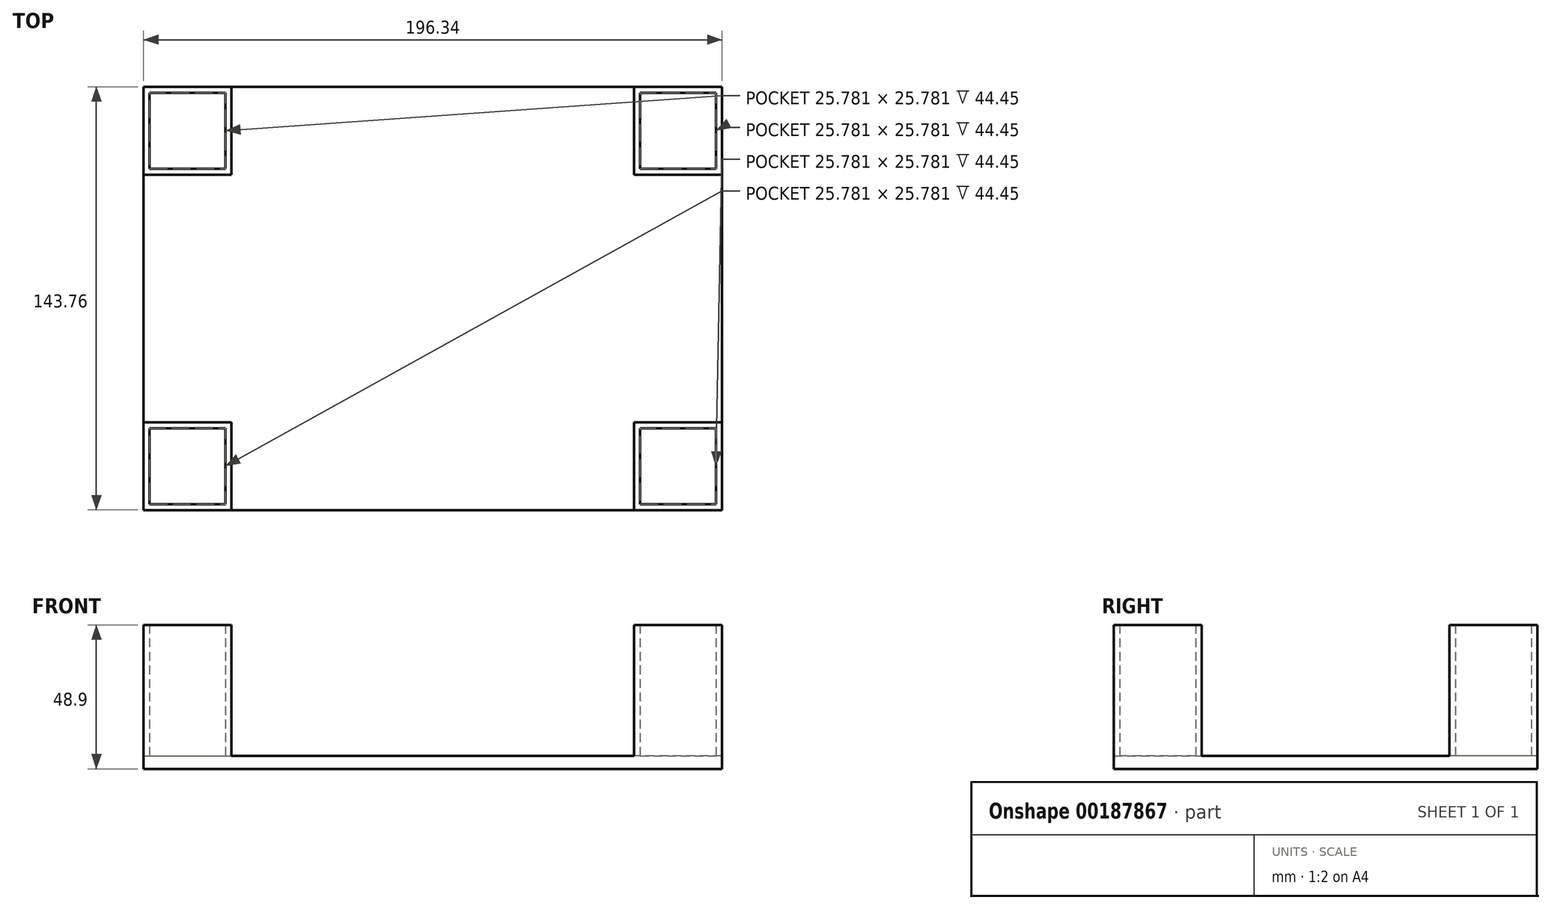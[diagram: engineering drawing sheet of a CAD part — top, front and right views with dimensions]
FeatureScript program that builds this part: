
annotation { "Feature Type Name" : "Feature", "Feature Type Description" : "" }
export const myFeature = defineFeature(function(context is Context, id is Id, definition is map)
    precondition{}
    {
        {
            var Q0;
            Q0=qCreatedBy(makeId("Top.planeOp"),FACE);
            var sketch = newSketch(context, id + "F0", { "sketchPlane" : qUnion([Q0])});
            skLineSegment(sketch, "E0.bottom", {"start": v(-88.52, 50.53) * mm, "end": v(107.82, 50.53) * mm});
            skLineSegment(sketch, "E0.top", {"start": v(-88.52, -93.23) * mm, "end": v(107.82, -93.23) * mm});
            skLineSegment(sketch, "E0.left", {"start": v(-88.52, 50.53) * mm, "end": v(-88.52, -93.23) * mm});
            skLineSegment(sketch, "E0.right", {"start": v(107.82, 50.53) * mm, "end": v(107.82, -93.23) * mm});
            skSolve(sketch);
        }
        {
            var Q0;
            Q0 = qSketchRegion(id + "F0", true);
            extrude(context, id + "F1", {"entities" : qUnion([Q0]), "depth" : 4.44 * mm});
        }
        {
            var Q0;
            Q0=makeQuery(id+"F1.opExtrude","CAP_FACE",FACE,{"disambiguationData":[OSD([sQuery(id+"F0.wireOp",EDGE,"E0.bottom"),sQuery(id+"F0.wireOp",EDGE,"E0.top"),sQuery(id+"F0.wireOp",EDGE,"E0.left"),sQuery(id+"F0.wireOp",EDGE,"E0.right")])],"isStart":false});
            var sketch = newSketch(context, id + "F2", { "sketchPlane" : qUnion([Q0])});
            skLineSegment(sketch, "E1.bottom", {"start": v(-88.52, 50.53) * mm, "end": v(-58.68, 50.53) * mm});
            skLineSegment(sketch, "E1.top", {"start": v(-88.52, 20.69) * mm, "end": v(-58.68, 20.69) * mm});
            skLineSegment(sketch, "E1.left", {"start": v(-88.52, 50.53) * mm, "end": v(-88.52, 20.69) * mm});
            skLineSegment(sketch, "E1.right", {"start": v(-58.68, 50.53) * mm, "end": v(-58.68, 20.69) * mm});
            skLineSegment(sketch, "E2.bottom", {"start": v(107.82, 50.53) * mm, "end": v(77.98, 50.53) * mm});
            skLineSegment(sketch, "E2.top", {"start": v(107.82, 20.69) * mm, "end": v(77.98, 20.69) * mm});
            skLineSegment(sketch, "E2.left", {"start": v(107.82, 50.53) * mm, "end": v(107.82, 20.69) * mm});
            skLineSegment(sketch, "E2.right", {"start": v(77.98, 50.53) * mm, "end": v(77.98, 20.69) * mm});
            skLineSegment(sketch, "E3.bottom", {"start": v(107.82, -93.23) * mm, "end": v(77.98, -93.23) * mm});
            skLineSegment(sketch, "E3.top", {"start": v(107.82, -63.39) * mm, "end": v(77.98, -63.39) * mm});
            skLineSegment(sketch, "E3.left", {"start": v(107.82, -93.23) * mm, "end": v(107.82, -63.39) * mm});
            skLineSegment(sketch, "E3.right", {"start": v(77.98, -93.23) * mm, "end": v(77.98, -63.39) * mm});
            skLineSegment(sketch, "E4.bottom", {"start": v(-88.52, -93.23) * mm, "end": v(-58.68, -93.23) * mm});
            skLineSegment(sketch, "E4.top", {"start": v(-88.52, -63.39) * mm, "end": v(-58.68, -63.39) * mm});
            skLineSegment(sketch, "E4.left", {"start": v(-88.52, -93.23) * mm, "end": v(-88.52, -63.39) * mm});
            skLineSegment(sketch, "E4.right", {"start": v(-58.68, -93.23) * mm, "end": v(-58.68, -63.39) * mm});
            skLineSegment(sketch, "E5.bottom", {"start": v(-86.49, 48.5) * mm, "end": v(-60.7, 48.5) * mm});
            skLineSegment(sketch, "E5.top", {"start": v(-86.49, 22.72) * mm, "end": v(-60.7, 22.72) * mm});
            skLineSegment(sketch, "E5.left", {"start": v(-86.49, 48.5) * mm, "end": v(-86.49, 22.72) * mm});
            skLineSegment(sketch, "E5.right", {"start": v(-60.7, 48.5) * mm, "end": v(-60.7, 22.72) * mm});
            skLineSegment(sketch, "E6.bottom", {"start": v(80, 48.5) * mm, "end": v(105.79, 48.5) * mm});
            skLineSegment(sketch, "E6.top", {"start": v(80, 22.72) * mm, "end": v(105.79, 22.72) * mm});
            skLineSegment(sketch, "E6.left", {"start": v(80, 48.5) * mm, "end": v(80, 22.72) * mm});
            skLineSegment(sketch, "E6.right", {"start": v(105.79, 48.5) * mm, "end": v(105.79, 22.72) * mm});
            skLineSegment(sketch, "E7.bottom", {"start": v(80, -65.42) * mm, "end": v(105.79, -65.42) * mm});
            skLineSegment(sketch, "E7.top", {"start": v(80, -91.2) * mm, "end": v(105.79, -91.2) * mm});
            skLineSegment(sketch, "E7.left", {"start": v(80, -65.42) * mm, "end": v(80, -91.2) * mm});
            skLineSegment(sketch, "E7.right", {"start": v(105.79, -65.42) * mm, "end": v(105.79, -91.2) * mm});
            skLineSegment(sketch, "E8.bottom", {"start": v(-86.49, -65.42) * mm, "end": v(-60.7, -65.42) * mm});
            skLineSegment(sketch, "E8.top", {"start": v(-86.49, -91.2) * mm, "end": v(-60.7, -91.2) * mm});
            skLineSegment(sketch, "E8.left", {"start": v(-86.49, -65.42) * mm, "end": v(-86.49, -91.2) * mm});
            skLineSegment(sketch, "E8.right", {"start": v(-60.7, -65.42) * mm, "end": v(-60.7, -91.2) * mm});
            skSolve(sketch);
        }
        {
            var Q0;
            Q0 = qSketchRegion(id + "F2", true);
            extrude(context, id + "F3", {"entities" : qUnion([Q0]), "operationType" : NewBodyOperationType.ADD, "depth" : 44.45 * mm});
        }
    });
